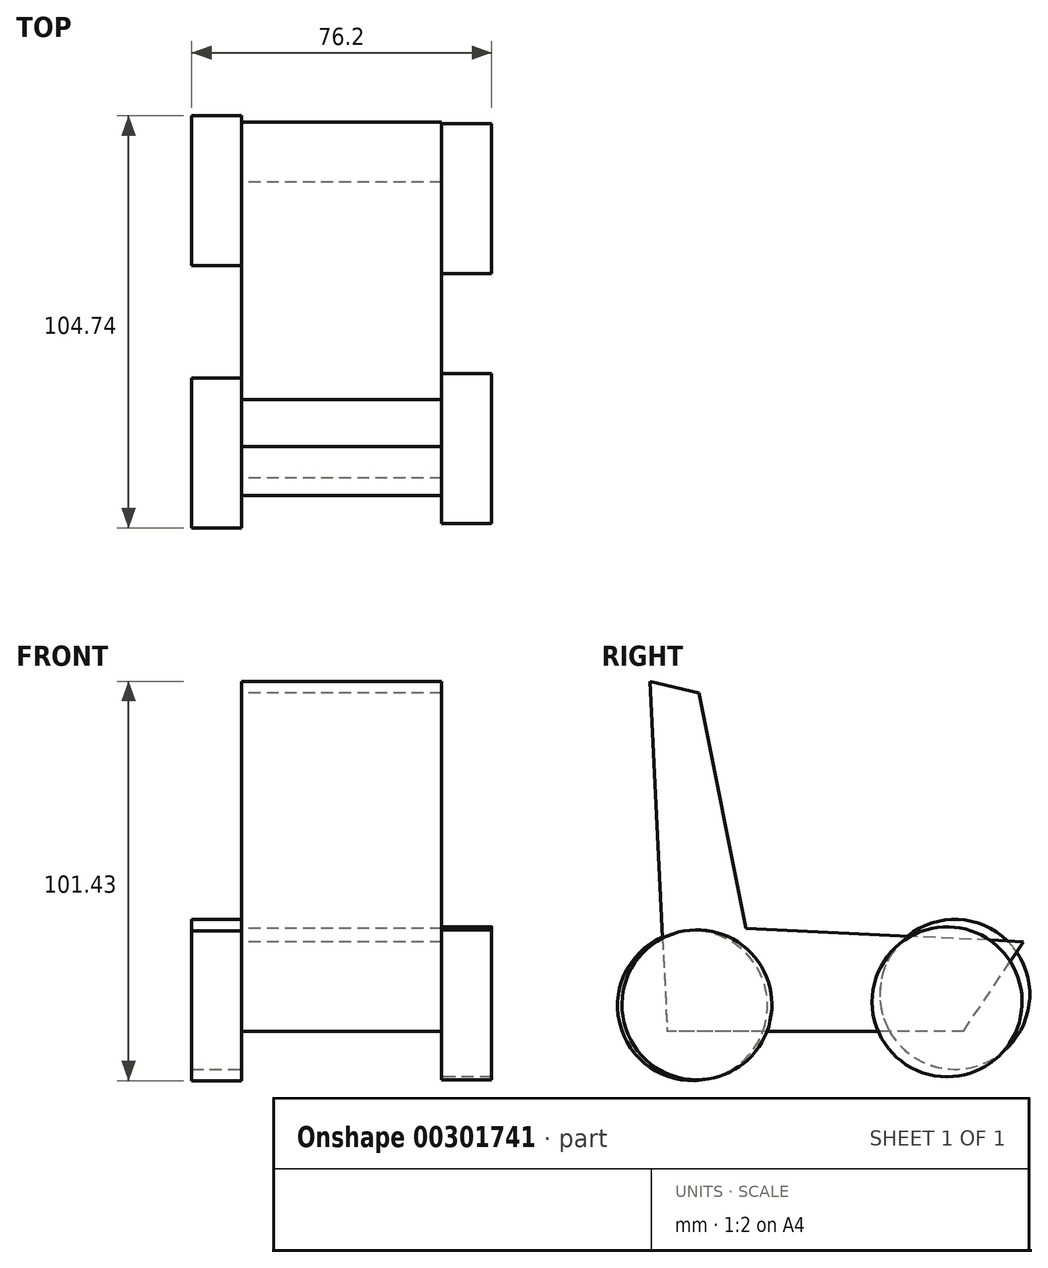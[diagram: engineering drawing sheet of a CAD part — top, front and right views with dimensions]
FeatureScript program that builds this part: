
annotation { "Feature Type Name" : "Feature", "Feature Type Description" : "" }
export const myFeature = defineFeature(function(context is Context, id is Id, definition is map)
    precondition{}
    {
        {
            var Q0;
            Q0=qCreatedBy(makeId("Right.planeOp"),FACE);
            var sketch = newSketch(context, id + "F0", { "sketchPlane" : qUnion([Q0])});
            skLineSegment(sketch, "E0", {"start": v(-43.16, 62.8) * mm, "end": v(-38.8, -26.06) * mm});
            skLineSegment(sketch, "E1", {"start": v(36.5, -26.06) * mm, "end": v(-38.8, -26.06) * mm});
            skLineSegment(sketch, "E2", {"start": v(36.5, -26.06) * mm, "end": v(51.66, -3.33) * mm});
            skLineSegment(sketch, "E3", {"start": v(51.66, -3.33) * mm, "end": v(-18.83, 0) * mm});
            skLineSegment(sketch, "E4", {"start": v(-18.83, 0) * mm, "end": v(-30.76, 59.8) * mm});
            skLineSegment(sketch, "E5", {"start": v(-30.76, 59.8) * mm, "end": v(-43.16, 62.8) * mm});
            skSolve(sketch);
        }
        {
            var Q0;
            Q0=makeQuery(id+"F0.imprint","IMPRINT",FACE,{"disambiguationData":[TD([[makeQuery(id+"F0.imprint","IMPRINT",EDGE,{"derivedFrom":sQuery(id+"F0.wireOp",EDGE,"E0")}),1.0]])]});
            extrude(context, id + "F1", {"entities" : qUnion([Q0]), "endBound" : BoundingType.SYMMETRIC, "depth" : 50.8 * mm});
        }
        {
            var Q0;
            Q0=makeQuery(id+"F1.opExtrude","CAP_FACE",FACE,{"disambiguationData":[OSD([sQuery(id+"F0.wireOp",EDGE,"E0"),sQuery(id+"F0.wireOp",EDGE,"E1"),sQuery(id+"F0.wireOp",EDGE,"E2"),sQuery(id+"F0.wireOp",EDGE,"E3"),sQuery(id+"F0.wireOp",EDGE,"E4"),sQuery(id+"F0.wireOp",EDGE,"E5")])],"isStart":false});
            var sketch = newSketch(context, id + "F2", { "sketchPlane" : qUnion([Q0])});
            skCircle(sketch, "E6", {"center": v(-31.26, -19.38) * mm, "radius": 19.05 * mm});
            skCircle(sketch, "E7", {"center": v(32.3, -18.6) * mm, "radius": 19.05 * mm});
            skSolve(sketch);
        }
        {
            var Q0;
            {var subQ0=sQuery(id+"F2.wireOp",EDGE,"E6");var subQ1=makeQuery(id+"F1.opExtrude","CAP_EDGE",EDGE,{"disambiguationData":[OSD([sQuery(id+"F0.wireOp",EDGE,"E0")])],"isStart":false});var subQ2=makeQuery(id+"F2.imprint","INTERSECT",VERTEX,{"derivedFrom":[subQ1,subQ0]});Q0=makeQuery(id+"F2.imprint","IMPRINT",FACE,{"disambiguationData":[TD([[makeQuery(id+"F2.imprint","IMPRINT",EDGE,{"disambiguationData":[TD([[subQ2,-1.0]])],"derivedFrom":subQ0}),1.0]])]});}
            var Q1;
            {var subQ3=sQuery(id+"F2.wireOp",EDGE,"E7");var subQ6=makeQuery(id+"F1.opExtrude","CAP_EDGE",EDGE,{"disambiguationData":[OSD([sQuery(id+"F0.wireOp",EDGE,"E3")])],"isStart":false});var subQ8=makeQuery(id+"F2.imprint","INTERSECT",VERTEX,{"disambiguationData":[OD(0.0)],"derivedFrom":[subQ6,subQ3]});Q1=makeQuery(id+"F2.imprint","IMPRINT",FACE,{"disambiguationData":[TD([[makeQuery(id+"F2.imprint","IMPRINT",EDGE,{"disambiguationData":[TD([[subQ8,1.0]])],"derivedFrom":subQ3}),1.0]])]});}
            var Q2;
            {var subQ0=sQuery(id+"F2.wireOp",EDGE,"E7");var subQ1=makeQuery(id+"F1.opExtrude","CAP_EDGE",EDGE,{"disambiguationData":[OSD([sQuery(id+"F0.wireOp",EDGE,"E2")])],"isStart":false});var subQ2=makeQuery(id+"F2.imprint","INTERSECT",VERTEX,{"derivedFrom":[subQ1,subQ0]});Q2=makeQuery(id+"F2.imprint","IMPRINT",FACE,{"disambiguationData":[TD([[makeQuery(id+"F2.imprint","IMPRINT",EDGE,{"disambiguationData":[TD([[subQ2,1.0]])],"derivedFrom":subQ0}),1.0]])]});}
            var Q3;
            {var subQ0=sQuery(id+"F2.wireOp",EDGE,"E7");var subQ1=makeQuery(id+"F1.opExtrude","CAP_EDGE",EDGE,{"disambiguationData":[OSD([sQuery(id+"F0.wireOp",EDGE,"E3")])],"isStart":false});var subQ2=makeQuery(id+"F2.imprint","INTERSECT",VERTEX,{"disambiguationData":[OD(0.0)],"derivedFrom":[subQ1,subQ0]});Q3=makeQuery(id+"F2.imprint","IMPRINT",FACE,{"disambiguationData":[TD([[makeQuery(id+"F2.imprint","IMPRINT",EDGE,{"disambiguationData":[TD([[subQ2,-1.0]])],"derivedFrom":subQ0}),1.0]])]});}
            var Q4;
            {var subQ0=sQuery(id+"F2.wireOp",EDGE,"E6");var subQ1=makeQuery(id+"F1.opExtrude","CAP_EDGE",EDGE,{"disambiguationData":[OSD([sQuery(id+"F0.wireOp",EDGE,"E0")])],"isStart":false});var subQ2=makeQuery(id+"F2.imprint","INTERSECT",VERTEX,{"derivedFrom":[subQ1,subQ0]});Q4=makeQuery(id+"F2.imprint","IMPRINT",FACE,{"disambiguationData":[TD([[makeQuery(id+"F2.imprint","IMPRINT",EDGE,{"disambiguationData":[TD([[subQ2,1.0]])],"derivedFrom":subQ0}),1.0]])]});}
            extrude(context, id + "F3", {"entities" : qUnion([Q0, Q1, Q2, Q3, Q4]), "operationType" : NewBodyOperationType.ADD, "depth" : 12.7 * mm});
        }
        {
            var Q0;
            Q0=makeQuery(id+"F1.opExtrude","CAP_FACE",FACE,{"disambiguationData":[OSD([sQuery(id+"F0.wireOp",EDGE,"E0"),sQuery(id+"F0.wireOp",EDGE,"E1"),sQuery(id+"F0.wireOp",EDGE,"E2"),sQuery(id+"F0.wireOp",EDGE,"E3"),sQuery(id+"F0.wireOp",EDGE,"E4"),sQuery(id+"F0.wireOp",EDGE,"E5")])],"isStart":true});
            var sketch = newSketch(context, id + "F4", { "sketchPlane" : qUnion([Q0])});
            skCircle(sketch, "E8", {"center": v(-34.27, -16.7) * mm, "radius": 19.05 * mm});
            skCircle(sketch, "E9", {"center": v(32.37, -19.6) * mm, "radius": 19.05 * mm});
            skSolve(sketch);
        }
        {
            var Q0;
            {var subQ0=sQuery(id+"F4.wireOp",EDGE,"E8");var subQ1=makeQuery(id+"F1.opExtrude","CAP_EDGE",EDGE,{"disambiguationData":[OSD([sQuery(id+"F0.wireOp",EDGE,"E2")])],"isStart":true});var subQ2=makeQuery(id+"F4.imprint","INTERSECT",VERTEX,{"derivedFrom":[subQ1,subQ0]});Q0=makeQuery(id+"F4.imprint","IMPRINT",FACE,{"disambiguationData":[TD([[makeQuery(id+"F4.imprint","IMPRINT",EDGE,{"disambiguationData":[TD([[subQ2,-1.0]])],"derivedFrom":subQ0}),1.0]])]});}
            var Q1;
            {var subQ3=sQuery(id+"F4.wireOp",EDGE,"E8");var subQ5=makeQuery(id+"F1.opExtrude","CAP_EDGE",EDGE,{"disambiguationData":[OSD([sQuery(id+"F0.wireOp",EDGE,"E3")])],"isStart":true});var subQ8=makeQuery(id+"F4.imprint","INTERSECT",VERTEX,{"disambiguationData":[OD(0.0)],"derivedFrom":[subQ5,subQ3]});Q1=makeQuery(id+"F4.imprint","IMPRINT",FACE,{"disambiguationData":[TD([[makeQuery(id+"F4.imprint","IMPRINT",EDGE,{"disambiguationData":[TD([[subQ8,-1.0]])],"derivedFrom":subQ3}),1.0]])]});}
            var Q2;
            {var subQ0=sQuery(id+"F4.wireOp",EDGE,"E8");var subQ1=makeQuery(id+"F1.opExtrude","CAP_EDGE",EDGE,{"disambiguationData":[OSD([sQuery(id+"F0.wireOp",EDGE,"E3")])],"isStart":true});var subQ2=makeQuery(id+"F4.imprint","INTERSECT",VERTEX,{"disambiguationData":[OD(0.0)],"derivedFrom":[subQ1,subQ0]});Q2=makeQuery(id+"F4.imprint","IMPRINT",FACE,{"disambiguationData":[TD([[makeQuery(id+"F4.imprint","IMPRINT",EDGE,{"disambiguationData":[TD([[subQ2,1.0]])],"derivedFrom":subQ0}),1.0]])]});}
            var Q3;
            {var subQ0=sQuery(id+"F4.wireOp",EDGE,"E9");var subQ1=makeQuery(id+"F1.opExtrude","CAP_EDGE",EDGE,{"disambiguationData":[OSD([sQuery(id+"F0.wireOp",EDGE,"E0")])],"isStart":true});var subQ2=makeQuery(id+"F4.imprint","INTERSECT",VERTEX,{"derivedFrom":[subQ1,subQ0]});Q3=makeQuery(id+"F4.imprint","IMPRINT",FACE,{"disambiguationData":[TD([[makeQuery(id+"F4.imprint","IMPRINT",EDGE,{"disambiguationData":[TD([[subQ2,-1.0]])],"derivedFrom":subQ0}),1.0]])]});}
            var Q4;
            {var subQ0=sQuery(id+"F4.wireOp",EDGE,"E9");var subQ1=makeQuery(id+"F1.opExtrude","CAP_EDGE",EDGE,{"disambiguationData":[OSD([sQuery(id+"F0.wireOp",EDGE,"E0")])],"isStart":true});var subQ2=makeQuery(id+"F4.imprint","INTERSECT",VERTEX,{"derivedFrom":[subQ1,subQ0]});Q4=makeQuery(id+"F4.imprint","IMPRINT",FACE,{"disambiguationData":[TD([[makeQuery(id+"F4.imprint","IMPRINT",EDGE,{"disambiguationData":[TD([[subQ2,1.0]])],"derivedFrom":subQ0}),1.0]])]});}
            extrude(context, id + "F5", {"entities" : qUnion([Q0, Q1, Q2, Q3, Q4]), "operationType" : NewBodyOperationType.ADD, "depth" : 12.7 * mm});
        }
    });
